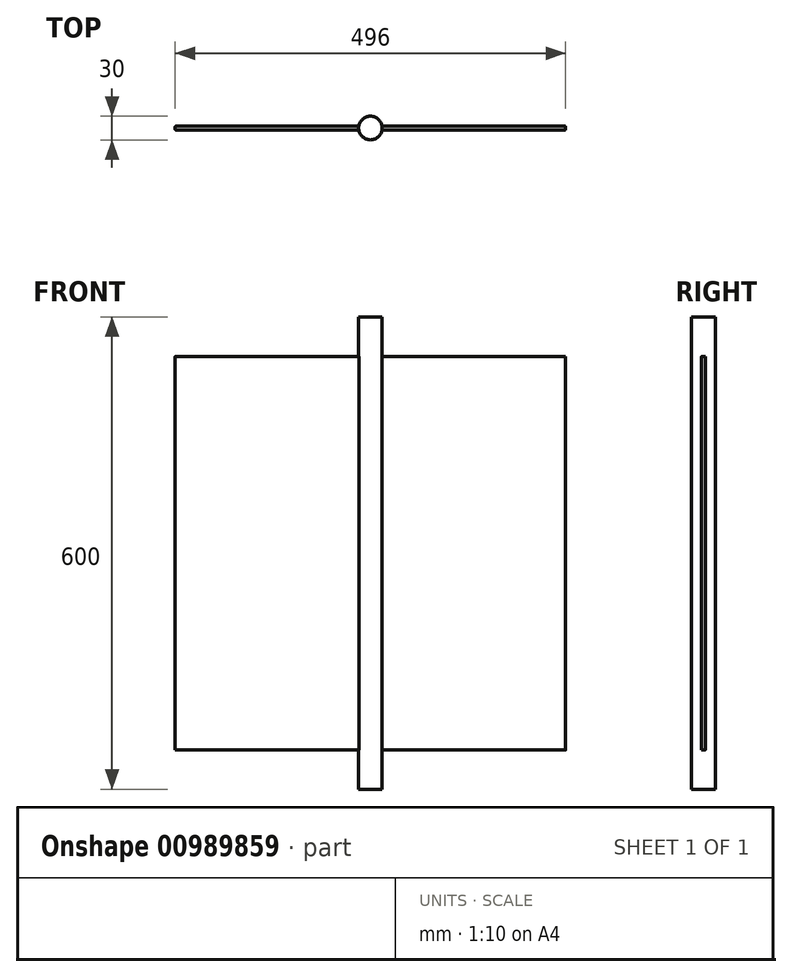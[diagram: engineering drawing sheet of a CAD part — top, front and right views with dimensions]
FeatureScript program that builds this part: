
annotation { "Feature Type Name" : "Feature", "Feature Type Description" : "" }
export const myFeature = defineFeature(function(context is Context, id is Id, definition is map)
    precondition{}
    {
        {
            var Q0;
            Q0=qCreatedBy(makeId("Top.planeOp"),FACE);
            var sketch = newSketch(context, id + "F0", { "sketchPlane" : qUnion([Q0])});
            skCircle(sketch, "E0", {"center": v(0, 0) * mm, "radius": 15 * mm});
            skSolve(sketch);
        }
        {
            var Q0;
            Q0 = qSketchRegion(id + "F0", true);
            extrude(context, id + "F1", {"entities" : qUnion([Q0]), "endBound" : BoundingType.SYMMETRIC, "depth" : 600 * mm, "offsetDistance" : 25 * mm});
        }
        {
            var Q0;
            Q0=qCreatedBy(makeId("Top.planeOp"),FACE);
            var sketch = newSketch(context, id + "F2", { "sketchPlane" : qUnion([Q0])});
            skLineSegment(sketch, "E1.bottom", {"start": v(-247, -2.5) * mm, "end": v(247, -2.5) * mm});
            skLineSegment(sketch, "E1.top", {"start": v(-247, 2.5) * mm, "end": v(247, 2.5) * mm});
            skLineSegment(sketch, "E1.left", {"start": v(-248, -1.5) * mm, "end": v(-248, 1.5) * mm});
            skLineSegment(sketch, "E1.right", {"start": v(248, -1.5) * mm, "end": v(248, 1.5) * mm});
            skPoint(sketch, "E2.visualSharp", {"position": v(-248, 2.5) * mm});
            skArc(sketch, "E2.filletArc", {"start": v(-247, 2.5) * mm, "mid": v(-247.7, 2.2) * mm, "end": v(-248, 1.5) * mm});
            skPoint(sketch, "E3.visualSharp", {"position": v(-248, -2.5) * mm});
            skArc(sketch, "E3.filletArc", {"start": v(-248, -1.5) * mm, "mid": v(-247.7, -2.2) * mm, "end": v(-247, -2.5) * mm});
            skPoint(sketch, "E4.visualSharp", {"position": v(248, 2.5) * mm});
            skArc(sketch, "E4.filletArc", {"start": v(248, 1.5) * mm, "mid": v(247.7, 2.2) * mm, "end": v(247, 2.5) * mm});
            skPoint(sketch, "E5.visualSharp", {"position": v(248, -2.5) * mm});
            skArc(sketch, "E5.filletArc", {"start": v(247, -2.5) * mm, "mid": v(247.7, -2.2) * mm, "end": v(248, -1.5) * mm});
            skSolve(sketch);
        }
        {
            var Q0;
            Q0 = qSketchRegion(id + "F2", true);
            extrude(context, id + "F3", {"entities" : qUnion([Q0]), "operationType" : NewBodyOperationType.ADD, "endBound" : BoundingType.SYMMETRIC, "depth" : 500 * mm, "offsetDistance" : 25 * mm});
        }
    });
